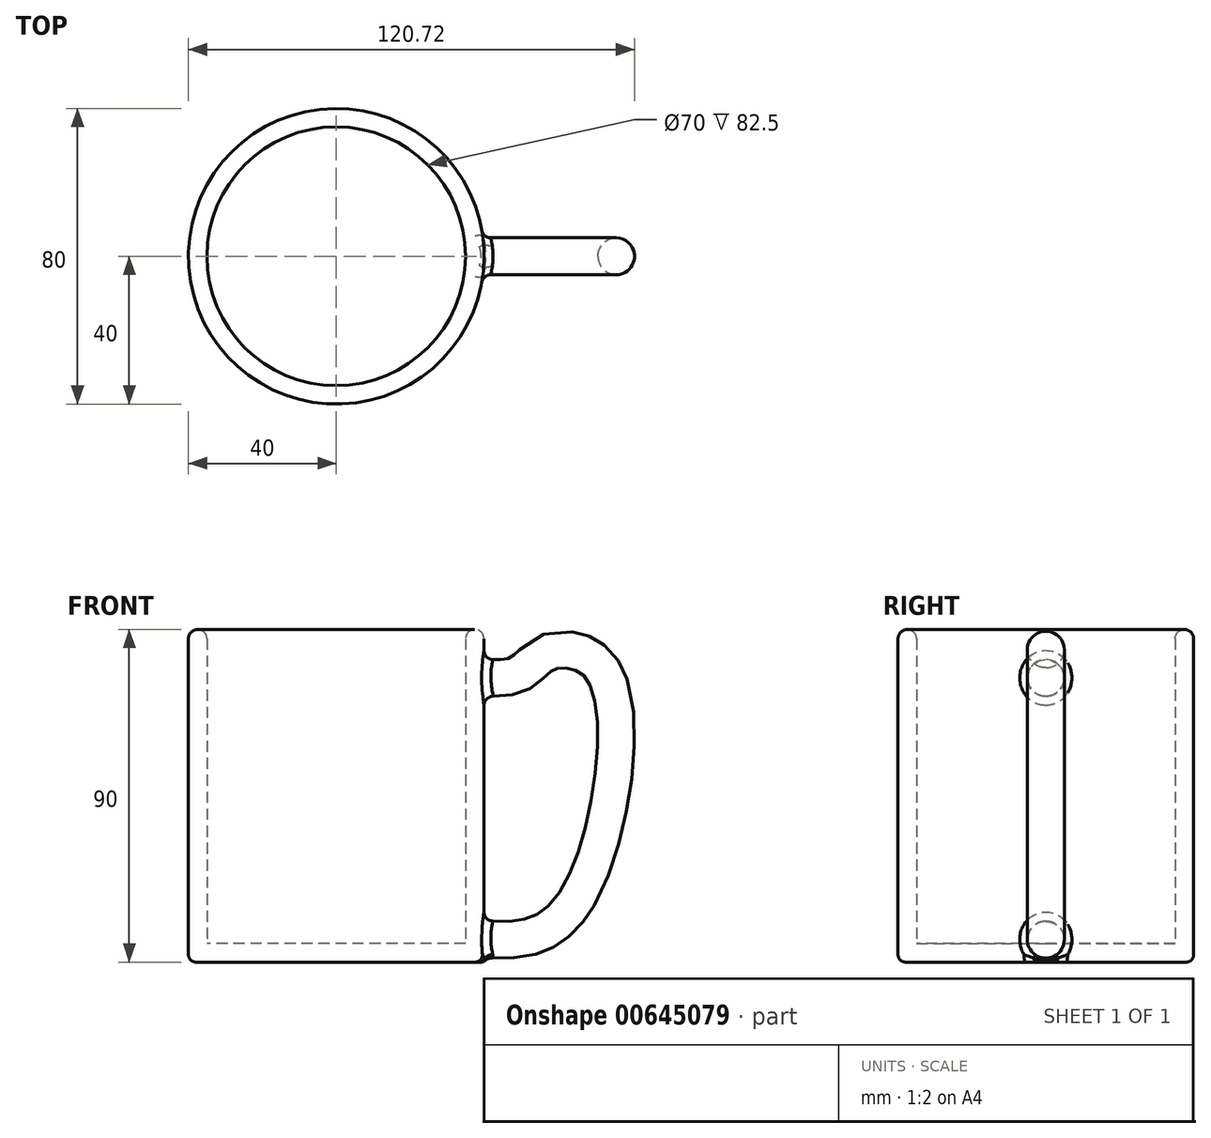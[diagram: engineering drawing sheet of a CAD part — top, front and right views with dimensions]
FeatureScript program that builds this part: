
annotation { "Feature Type Name" : "Feature", "Feature Type Description" : "" }
export const myFeature = defineFeature(function(context is Context, id is Id, definition is map)
    precondition{}
    {
        {
            var Q0;
            Q0=qCreatedBy(makeId("Top.planeOp"),FACE);
            var sketch = newSketch(context, id + "F0", { "sketchPlane" : qUnion([Q0])});
            skCircle(sketch, "E0", {"center": v(0, 0) * mm, "radius": 40 * mm});
            skSolve(sketch);
        }
        {
            var Q0;
            Q0 = qSketchRegion(id + "F0", true);
            extrude(context, id + "F1", {"entities" : qUnion([Q0]), "depth" : 90 * mm, "offsetDistance" : 25 * mm});
        }
        {
            var Q0;
            Q0=qCreatedBy(makeId("Front.planeOp"),FACE);
            var sketch = newSketch(context, id + "F2", { "sketchPlane" : qUnion([Q0])});
            skFitSpline(sketch, "E1", {"points": [v(31.53, 77.69) * mm, v(49.3, 77.48) * mm, v(57.16, 83.27) * mm, v(70.6, 80.17) * mm, v(73.08, 41.1) * mm, v(57.37, 9.46) * mm, v(35.04, 7.19) * mm], "startDerivative": vector(135.78, -20.8) * mm, "endDerivative": vector(-142.53, 14.7) * mm});
            skSolve(sketch);
        }
        {
            var Q0;
            Q0=qCreatedBy(makeId("Right.planeOp"),FACE);
            cPlane(context, id + "F3", {"entities" : qUnion([Q0]), "cplaneType" : CPlaneType.OFFSET, "offset" : 35.2 * mm, "width" : 150 * mm, "height" : 150 * mm});
        }
        {
            var Q0;
            Q0=qCreatedBy(id+"F3.planeOp",FACE);
            var sketch = newSketch(context, id + "F4", { "sketchPlane" : qUnion([Q0])});
            skCircle(sketch, "E2", {"center": v(0, 77.6) * mm, "radius": 5 * mm});
            skSolve(sketch);
        }
        {
            var Q0;
            Q0 = qSketchRegion(id + "F4", true);
            var Q1;
            Q1=sQuery(id+"F4.wireOp",EDGE,"E2");
            var Q2;
            Q2=sQuery(id+"F4.wireOp",EDGE,"JQA93nCC-xFb6-pvDL-1zCd-Vx9kST2zEbLq");
            var Q3;
            Q3=sQuery(id+"F2.wireOp",EDGE,"E1");
            sweep(context, id + "F5", {"operationType" : NewBodyOperationType.ADD, "profiles" : qUnion([Q0]), "surfaceProfiles" : qUnion([Q1, Q2]), "path" : qUnion([Q3])});
        }
        {
            var Q0;
            Q0=makeQuery(id+"F1.opExtrude","CAP_FACE",FACE,{"disambiguationData":[OSD([sQuery(id+"F0.wireOp",EDGE,"E0")])],"isStart":false});
            shell(context, id + "F6", {"entities" : qUnion([Q0]), "thickness" : 5 * mm});
        }
        {
            var Q0;
            Q0=makeQuery(id+"F1.opExtrude","CAP_EDGE",EDGE,{"disambiguationData":[OSD([sQuery(id+"F0.wireOp",EDGE,"E0")])],"isStart":false});
            var Q1;
            Q1=makeQuery(id+"F5.opSweep","SWEPT_FACE",FACE,{"disambiguationData":[OSD([sQuery(id+"F2.wireOp",EDGE,"E1"),sQuery(id+"F4.wireOp",EDGE,"E2")])]});
            fillet(context, id + "F7", {"entities" : qUnion([Q0, Q1]), "radius" : 2.5 * mm, "tangentPropagation" : true, "allowEdgeOverflow" : false});
        }
        {
            var Q0;
            {var subQ0=sQuery(id+"F0.wireOp",EDGE,"E0");Q0=makeQuery(id+"F6.opShell","OFFSET_EDGE",EDGE,{"disambiguationData":[OSD([subQ0]),TDD([makeQuery(id+"F1.opExtrude","CAP_EDGE",EDGE,{"disambiguationData":[OSD([subQ0])],"isStart":false})])]});}
            fillet(context, id + "F8", {"entities" : qUnion([Q0]), "radius" : 2.5 * mm, "tangentPropagation" : true, "allowEdgeOverflow" : false});
        }
        {
            var Q0;
            Q0=makeQuery(id+"F5.boolean.opBoolean","INTERSECT",EDGE,{"disambiguationData":[OD(1.0)],"derivedFrom":[makeQuery(id+"F1.opExtrude","SWEPT_FACE",FACE,{"disambiguationData":[OSD([sQuery(id+"F0.wireOp",EDGE,"E0")])]}),makeQuery(id+"F5.opSweep","SWEPT_FACE",FACE,{"disambiguationData":[OSD([sQuery(id+"F2.wireOp",EDGE,"E1"),sQuery(id+"F4.wireOp",EDGE,"E2")])]})]});
            var Q1;
            Q1=makeQuery(id+"F1.opExtrude","CAP_EDGE",EDGE,{"disambiguationData":[OSD([sQuery(id+"F0.wireOp",EDGE,"E0")])],"isStart":true});
            var Q2;
            {var subQ0=sQuery(id+"F0.wireOp",EDGE,"E0");Q2=makeQuery(id+"F7.opFillet","BLEND_EDGE",EDGE,{"blendedFrom":[makeQuery(id+"F1.opExtrude","CAP_EDGE",EDGE,{"disambiguationData":[OSD([subQ0])],"isStart":false}),makeQuery(id+"F1.opExtrude","SWEPT_FACE",FACE,{"disambiguationData":[OSD([subQ0])]})],"blendedInto":[makeQuery(id+"F1.opExtrude","SWEPT_FACE",FACE,{"disambiguationData":[OSD([subQ0])]})]});}
            var Q3;
            {var subQ0=sQuery(id+"F0.wireOp",EDGE,"E0");Q3=makeQuery(id+"F8.opFillet","BLEND_EDGE",EDGE,{"blendedFrom":[makeQuery(id+"F6.opShell","OFFSET_EDGE",EDGE,{"disambiguationData":[OSD([subQ0]),TDD([makeQuery(id+"F1.opExtrude","CAP_EDGE",EDGE,{"disambiguationData":[OSD([subQ0])],"isStart":false})])]}),makeQuery(id+"F7.opFillet","BLEND_FACE",FACE,{"disambiguationData":[OSD([subQ0])]})],"blendedInto":[makeQuery(id+"F7.opFillet","BLEND_FACE",FACE,{"disambiguationData":[OSD([subQ0])]})]});}
            fillet(context, id + "F9", {"entities" : qUnion([Q0, Q1, Q2, Q3]), "radius" : 2 * mm, "tangentPropagation" : true, "allowEdgeOverflow" : false});
        }
    });
